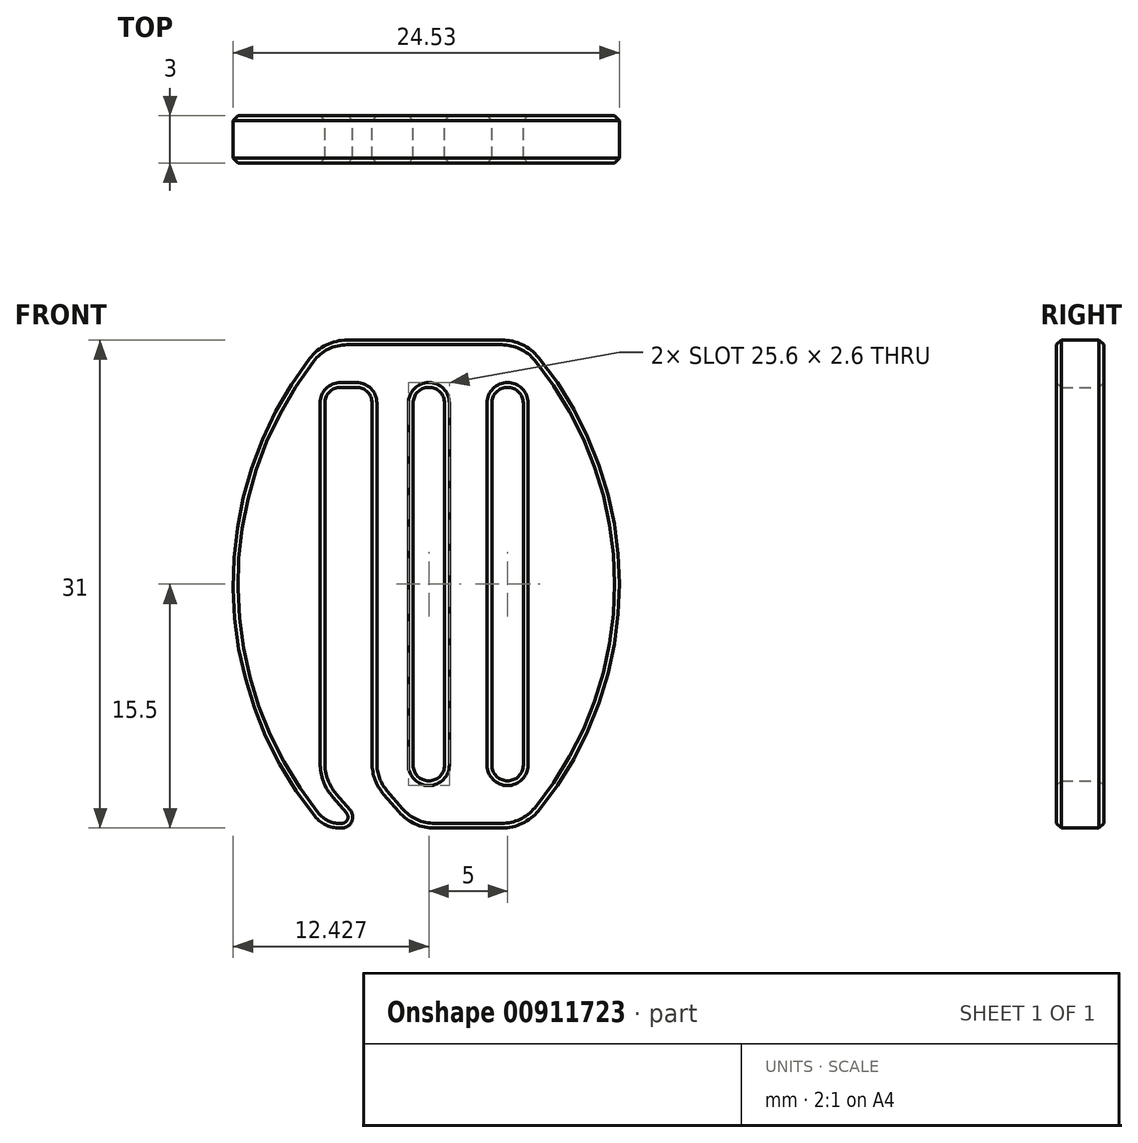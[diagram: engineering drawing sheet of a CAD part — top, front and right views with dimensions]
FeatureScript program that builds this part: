
annotation { "Feature Type Name" : "Feature", "Feature Type Description" : "" }
export const myFeature = defineFeature(function(context is Context, id is Id, definition is map)
    precondition{}
    {
        {
            var Q0;
            Q0=qCreatedBy(makeId("Front.planeOp"),FACE);
            var sketch = newSketch(context, id + "F0", { "sketchPlane" : qUnion([Q0])});
            skLineSegment(sketch, "E0.bottom", {"start": v(15.5, 22.44) * mm, "end": v(15.5, 22.44) * mm});
            skLineSegment(sketch, "E0.top", {"start": v(15.5, -2.56) * mm, "end": v(15.5, -2.56) * mm});
            skLineSegment(sketch, "E0.left", {"start": v(14.5, 21.44) * mm, "end": v(14.5, -1.56) * mm});
            skLineSegment(sketch, "E0.right", {"start": v(16.5, 21.44) * mm, "end": v(16.5, -2.56) * mm});
            skLineSegment(sketch, "E1.1.0.1", {"start": v(11.5, 21.44) * mm, "end": v(11.5, -1.56) * mm});
            skLineSegment(sketch, "E1.1.0.2", {"start": v(9.5, 21.44) * mm, "end": v(9.5, -1.56) * mm});
            skLineSegment(sketch, "E1.1.0.3", {"start": v(10.5, -2.56) * mm, "end": v(10.5, -2.56) * mm});
            skLineSegment(sketch, "E1.direction1", {"start": v(10.5, 22.44) * mm, "end": v(10.5, 22.44) * mm});
            skLineSegment(sketch, "E2", {"start": v(10.87, -5.56) * mm, "end": v(15.14, -5.56) * mm});
            skLineSegment(sketch, "E3", {"start": v(2.11, 9.94) * mm, "end": v(37.93, 9.94) * mm, "construction": true});
            skLineSegment(sketch, "E4.MirrorCS", {"start": v(9.5, 25.44) * mm, "end": v(15.14, 25.44) * mm});
            skArc(sketch, "E5", {"start": v(17.46, -4.46) * mm, "mid": v(22.6, 9.94) * mm, "end": v(17.46, 24.34) * mm});
            skPoint(sketch, "E6.visualSharp", {"position": v(16.5, 25.44) * mm});
            skArc(sketch, "E6.filletArc", {"start": v(17.46, 24.34) * mm, "mid": v(16.42, 25.15) * mm, "end": v(15.14, 25.44) * mm});
            skPoint(sketch, "E7.visualSharp", {"position": v(16.5, -5.56) * mm});
            skArc(sketch, "E7.filletArc", {"start": v(15.14, -5.56) * mm, "mid": v(16.42, -5.27) * mm, "end": v(17.46, -4.46) * mm});
            skLineSegment(sketch, "E8", {"start": v(6.9, 21.44) * mm, "end": v(6.9, -1.44) * mm});
            skLineSegment(sketch, "E9", {"start": v(8.6, -4.53) * mm, "end": v(7.63, -3.4) * mm});
            skPoint(sketch, "E10.visualSharp", {"position": v(6.9, -2.56) * mm});
            skArc(sketch, "E10.filletArc", {"start": v(6.9, -1.44) * mm, "mid": v(7.08, -2.49) * mm, "end": v(7.63, -3.4) * mm});
            skPoint(sketch, "E11.visualSharp", {"position": v(9.5, -5.56) * mm});
            skArc(sketch, "E11.filletArc", {"start": v(8.6, -4.53) * mm, "mid": v(9.62, -5.29) * mm, "end": v(10.87, -5.56) * mm});
            skLineSegment(sketch, "E12", {"start": v(5.9, 22.44) * mm, "end": v(4.9, 22.44) * mm});
            skLineSegment(sketch, "E13", {"start": v(3.9, 21.44) * mm, "end": v(3.9, -1.44) * mm});
            skLineSegment(sketch, "E14", {"start": v(4.6, -1.44) * mm, "end": v(11.2, -9.04) * mm, "construction": true});
            skLineSegment(sketch, "E15", {"start": v(4.63, -3.4) * mm, "end": v(5.5, -4.4) * mm});
            skPoint(sketch, "E16.visualSharp", {"position": v(3.9, -2.56) * mm});
            skArc(sketch, "E16.filletArc", {"start": v(3.9, -1.44) * mm, "mid": v(4.08, -2.49) * mm, "end": v(4.63, -3.4) * mm});
            skLineSegment(sketch, "E17", {"start": v(9.5, 25.44) * mm, "end": v(5.3, 25.44) * mm});
            skLineSegment(sketch, "E18", {"start": v(4.96, -5.56) * mm, "end": v(4.82, -5.56) * mm});
            skPoint(sketch, "E19.visualSharp", {"position": v(6.5, -5.56) * mm});
            skArc(sketch, "E19.filletArc", {"start": v(4.96, -5.56) * mm, "mid": v(5.6, -5.15) * mm, "end": v(5.5, -4.4) * mm});
            skArc(sketch, "E20", {"start": v(2.93, 24.27) * mm, "mid": v(-1.93, 9.67) * mm, "end": v(3.27, -4.81) * mm});
            skPoint(sketch, "E21.visualSharp", {"position": v(3.9, 25.44) * mm});
            skArc(sketch, "E21.filletArc", {"start": v(5.3, 25.44) * mm, "mid": v(3.98, 25.13) * mm, "end": v(2.93, 24.27) * mm});
            skPoint(sketch, "E22.visualSharp", {"position": v(3.9, -5.56) * mm});
            skArc(sketch, "E22.filletArc", {"start": v(3.27, -4.81) * mm, "mid": v(3.96, -5.36) * mm, "end": v(4.82, -5.56) * mm});
            skPoint(sketch, "E23.visualSharp", {"position": v(6.9, 22.44) * mm});
            skArc(sketch, "E23.filletArc", {"start": v(6.9, 21.44) * mm, "mid": v(6.6, 22.15) * mm, "end": v(5.9, 22.44) * mm});
            skPoint(sketch, "E24.visualSharp", {"position": v(3.9, 22.44) * mm});
            skArc(sketch, "E24.filletArc", {"start": v(4.9, 22.44) * mm, "mid": v(4.18, 22.15) * mm, "end": v(3.9, 21.44) * mm});
            skPoint(sketch, "E25.visualSharp", {"position": v(9.5, 22.44) * mm});
            skArc(sketch, "E25.filletArc", {"start": v(10.5, 22.44) * mm, "mid": v(9.8, 22.15) * mm, "end": v(9.5, 21.44) * mm});
            skPoint(sketch, "E26.newPointA", {"position": v(11.5, 22.44) * mm});
            skPoint(sketch, "E26.newPointB", {"position": v(14.5, 22.44) * mm});
            skArc(sketch, "E26.filletArc", {"start": v(11.5, 21.44) * mm, "mid": v(11.2, 22.15) * mm, "end": v(10.5, 22.44) * mm});
            skPoint(sketch, "E27.visualSharp", {"position": v(9.5, -2.56) * mm});
            skArc(sketch, "E27.filletArc", {"start": v(9.5, -1.56) * mm, "mid": v(9.8, -2.27) * mm, "end": v(10.5, -2.56) * mm});
            skPoint(sketch, "E28.visualSharp", {"position": v(11.5, -2.56) * mm});
            skArc(sketch, "E28.filletArc", {"start": v(10.5, -2.56) * mm, "mid": v(11.2, -2.27) * mm, "end": v(11.5, -1.56) * mm});
            skPoint(sketch, "E29.visualSharp", {"position": v(14.5, -2.56) * mm});
            skArc(sketch, "E29.filletArc", {"start": v(14.5, -1.56) * mm, "mid": v(14.8, -2.27) * mm, "end": v(15.5, -2.56) * mm});
            skPoint(sketch, "E30.newPointA", {"position": v(16.5, -2.56) * mm});
            skArc(sketch, "E30.filletArc", {"start": v(15.5, -2.56) * mm, "mid": v(16.2, -2.27) * mm, "end": v(16.5, -1.56) * mm});
            skArc(sketch, "E31.filletArc", {"start": v(15.5, 22.44) * mm, "mid": v(14.8, 22.15) * mm, "end": v(14.5, 21.44) * mm});
            skPoint(sketch, "E32.visualSharp", {"position": v(16.5, 22.44) * mm});
            skArc(sketch, "E33.filletArc", {"start": v(16.5, 21.44) * mm, "mid": v(16.2, 22.15) * mm, "end": v(15.5, 22.44) * mm});
            skSolve(sketch);
        }
        {
            var Q0;
            Q0=makeQuery(id+"F0.imprint","IMPRINT",FACE,{"disambiguationData":[TD([[makeQuery(id+"F0.imprint","IMPRINT",EDGE,{"derivedFrom":sQuery(id+"F0.wireOp",EDGE,"E0.left")}),-1.0]])]});
            extrude(context, id + "F1", {"entities" : qUnion([Q0]), "depth" : 3 * mm, "offsetDistance" : 25 * mm});
        }
        {
            var Q0;
            Q0=makeQuery(id+"F1.opExtrude","CAP_FACE",FACE,{"disambiguationData":[OSD([sQuery(id+"F0.wireOp",EDGE,"E0.bottom"),sQuery(id+"F0.wireOp",EDGE,"E0.top"),sQuery(id+"F0.wireOp",EDGE,"E0.left"),sQuery(id+"F0.wireOp",EDGE,"E0.right"),sQuery(id+"F0.wireOp",EDGE,"E1.1.0.0"),sQuery(id+"F0.wireOp",EDGE,"E1.1.0.1"),sQuery(id+"F0.wireOp",EDGE,"E1.1.0.2"),sQuery(id+"F0.wireOp",EDGE,"E1.1.0.3"),sQuery(id+"F0.wireOp",EDGE,"E2"),sQuery(id+"F0.wireOp",EDGE,"E4.MirrorCS"),sQuery(id+"F0.wireOp",EDGE,"E5"),sQuery(id+"F0.wireOp",EDGE,"E6.filletArc"),sQuery(id+"F0.wireOp",EDGE,"E7.filletArc"),sQuery(id+"F0.wireOp",EDGE,"E8"),sQuery(id+"F0.wireOp",EDGE,"E9"),sQuery(id+"F0.wireOp",EDGE,"E10.filletArc"),sQuery(id+"F0.wireOp",EDGE,"E11.filletArc"),sQuery(id+"F0.wireOp",EDGE,"E12"),sQuery(id+"F0.wireOp",EDGE,"E13"),sQuery(id+"F0.wireOp",EDGE,"E15"),sQuery(id+"F0.wireOp",EDGE,"E16.filletArc"),sQuery(id+"F0.wireOp",EDGE,"E17"),sQuery(id+"F0.wireOp",EDGE,"E18"),sQuery(id+"F0.wireOp",EDGE,"E19.filletArc"),sQuery(id+"F0.wireOp",EDGE,"E20"),sQuery(id+"F0.wireOp",EDGE,"E21.filletArc"),sQuery(id+"F0.wireOp",EDGE,"E22.filletArc")])],"isStart":false});
            var Q1;
            Q1=makeQuery(id+"F1.opExtrude","CAP_FACE",FACE,{"disambiguationData":[OSD([sQuery(id+"F0.wireOp",EDGE,"E0.bottom"),sQuery(id+"F0.wireOp",EDGE,"E0.top"),sQuery(id+"F0.wireOp",EDGE,"E0.left"),sQuery(id+"F0.wireOp",EDGE,"E0.right"),sQuery(id+"F0.wireOp",EDGE,"E1.1.0.0"),sQuery(id+"F0.wireOp",EDGE,"E1.1.0.1"),sQuery(id+"F0.wireOp",EDGE,"E1.1.0.2"),sQuery(id+"F0.wireOp",EDGE,"E1.1.0.3"),sQuery(id+"F0.wireOp",EDGE,"E2"),sQuery(id+"F0.wireOp",EDGE,"E4.MirrorCS"),sQuery(id+"F0.wireOp",EDGE,"E5"),sQuery(id+"F0.wireOp",EDGE,"E6.filletArc"),sQuery(id+"F0.wireOp",EDGE,"E7.filletArc"),sQuery(id+"F0.wireOp",EDGE,"E8"),sQuery(id+"F0.wireOp",EDGE,"E9"),sQuery(id+"F0.wireOp",EDGE,"E10.filletArc"),sQuery(id+"F0.wireOp",EDGE,"E11.filletArc"),sQuery(id+"F0.wireOp",EDGE,"E12"),sQuery(id+"F0.wireOp",EDGE,"E13"),sQuery(id+"F0.wireOp",EDGE,"E15"),sQuery(id+"F0.wireOp",EDGE,"E16.filletArc"),sQuery(id+"F0.wireOp",EDGE,"E17"),sQuery(id+"F0.wireOp",EDGE,"E18"),sQuery(id+"F0.wireOp",EDGE,"E19.filletArc"),sQuery(id+"F0.wireOp",EDGE,"E20"),sQuery(id+"F0.wireOp",EDGE,"E21.filletArc"),sQuery(id+"F0.wireOp",EDGE,"E22.filletArc")])],"isStart":true});
            chamfer(context, id + "F2", {"entities" : qUnion([Q0, Q1]), "width" : 0.3 * mm, "tangentPropagation" : true});
        }
    });
